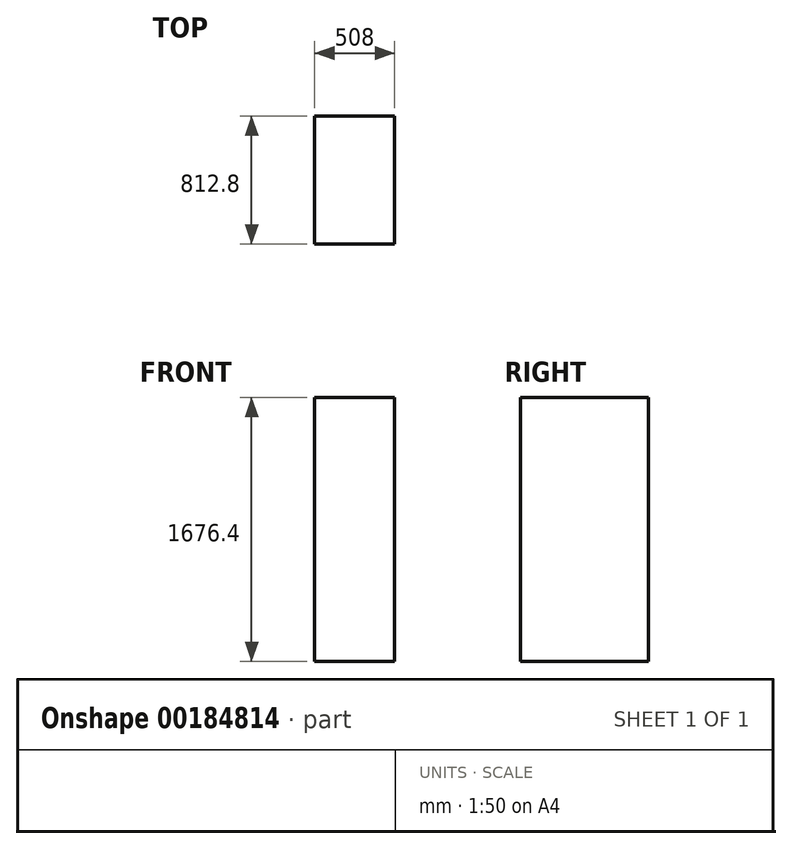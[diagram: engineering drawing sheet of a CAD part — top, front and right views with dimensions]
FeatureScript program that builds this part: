
annotation { "Feature Type Name" : "Feature", "Feature Type Description" : "" }
export const myFeature = defineFeature(function(context is Context, id is Id, definition is map)
    precondition{}
    {
        {
            var Q0;
            Q0=qCreatedBy(makeId("Top.planeOp"),FACE);
            var sketch = newSketch(context, id + "F0", { "sketchPlane" : qUnion([Q0])});
            skLineSegment(sketch, "E0.bottom", {"start": v(254, -406.4) * mm, "end": v(-254, -406.4) * mm});
            skLineSegment(sketch, "E0.top", {"start": v(254, 406.4) * mm, "end": v(-254, 406.4) * mm});
            skLineSegment(sketch, "E0.left", {"start": v(254, -406.4) * mm, "end": v(254, 406.4) * mm});
            skLineSegment(sketch, "E0.right", {"start": v(-254, -406.4) * mm, "end": v(-254, 406.4) * mm});
            skPoint(sketch, "E0.middle", {"position": v(0, 0) * mm});
            skSolve(sketch);
        }
        {
            var Q0;
            Q0 = qSketchRegion(id + "F0", true);
            extrude(context, id + "F1", {"entities" : qUnion([Q0]), "depth" : 1676.4 * mm});
        }
    });
